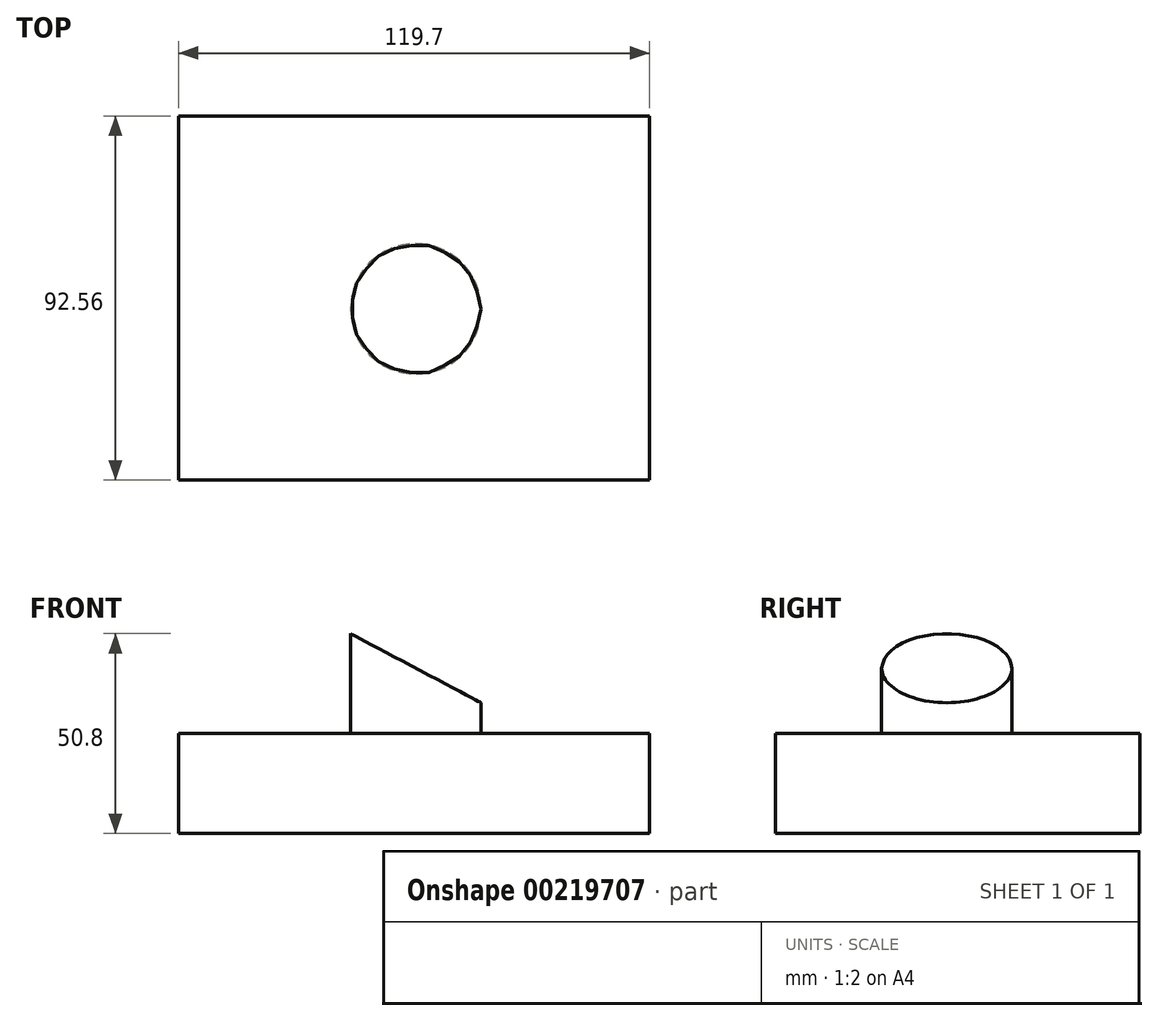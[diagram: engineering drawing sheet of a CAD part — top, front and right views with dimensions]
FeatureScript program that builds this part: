
annotation { "Feature Type Name" : "Feature", "Feature Type Description" : "" }
export const myFeature = defineFeature(function(context is Context, id is Id, definition is map)
    precondition{}
    {
        {
            var Q0;
            Q0=qCreatedBy(makeId("Top.planeOp"),FACE);
            var sketch = newSketch(context, id + "F0", { "sketchPlane" : qUnion([Q0])});
            skLineSegment(sketch, "E0.bottom", {"start": v(-60.3, 49.03) * mm, "end": v(59.39, 49.03) * mm});
            skLineSegment(sketch, "E0.top", {"start": v(-60.3, -43.53) * mm, "end": v(59.39, -43.53) * mm});
            skLineSegment(sketch, "E0.left", {"start": v(-60.3, 49.03) * mm, "end": v(-60.3, -43.53) * mm});
            skLineSegment(sketch, "E0.right", {"start": v(59.39, 49.03) * mm, "end": v(59.39, -43.53) * mm});
            skSolve(sketch);
        }
        {
            var Q0;
            Q0=makeQuery(id+"F0.imprint","IMPRINT",FACE,{"disambiguationData":[TD([[makeQuery(id+"F0.imprint","IMPRINT",EDGE,{"derivedFrom":sQuery(id+"F0.wireOp",EDGE,"E0.bottom")}),-1.0]])]});
            extrude(context, id + "F1", {"entities" : qUnion([Q0]), "depth" : 25.4 * mm});
        }
        {
            var Q0;
            Q0=makeQuery(id+"F1.opExtrude","CAP_FACE",FACE,{"disambiguationData":[OSD([sQuery(id+"F0.wireOp",EDGE,"E0.bottom"),sQuery(id+"F0.wireOp",EDGE,"E0.top"),sQuery(id+"F0.wireOp",EDGE,"E0.left"),sQuery(id+"F0.wireOp",EDGE,"E0.right")])],"isStart":false});
            var sketch = newSketch(context, id + "F2", { "sketchPlane" : qUnion([Q0])});
            skCircle(sketch, "E1", {"center": v(0, 0) * mm, "radius": 16.55 * mm});
            skSolve(sketch);
        }
        {
            var Q0;
            Q0 = qSketchRegion(id + "F2", true);
            extrude(context, id + "F3", {"entities" : qUnion([Q0]), "operationType" : NewBodyOperationType.ADD, "depth" : 25.4 * mm});
        }
        {
            var Q0;
            Q0=makeQuery(id+"F1.opExtrude","SWEPT_FACE",FACE,{"disambiguationData":[OSD([sQuery(id+"F0.wireOp",EDGE,"E0.top")])]});
            var sketch = newSketch(context, id + "F4", { "sketchPlane" : qUnion([Q0])});
            skLineSegment(sketch, "E2.0", {"start": v(-16.55, 50.8) * mm, "end": v(16.55, 50.8) * mm});
            skLineSegment(sketch, "E3", {"start": v(16.55, 50.8) * mm, "end": v(16.55, 25.4) * mm});
            skLineSegment(sketch, "E4", {"start": v(-16.55, 50.8) * mm, "end": v(16.55, 33.27) * mm});
            skSolve(sketch);
        }
        {
            var Q0;
            {var subQ0=sQuery(id+"F4.wireOp",EDGE,"E2.0");Q0=makeQuery(id+"F4.imprint","IMPRINT",FACE,{"disambiguationData":[TD([[makeQuery(id+"F4.imprint","IMPRINT",EDGE,{"derivedFrom":subQ0}),-1.0]])]});}
            extrude(context, id + "F5", {"entities" : qUnion([Q0]), "operationType" : NewBodyOperationType.REMOVE, "endBound" : BoundingType.THROUGH_ALL, "oppositeDirection" : true, "depth" : 25.4 * mm});
        }
    });
